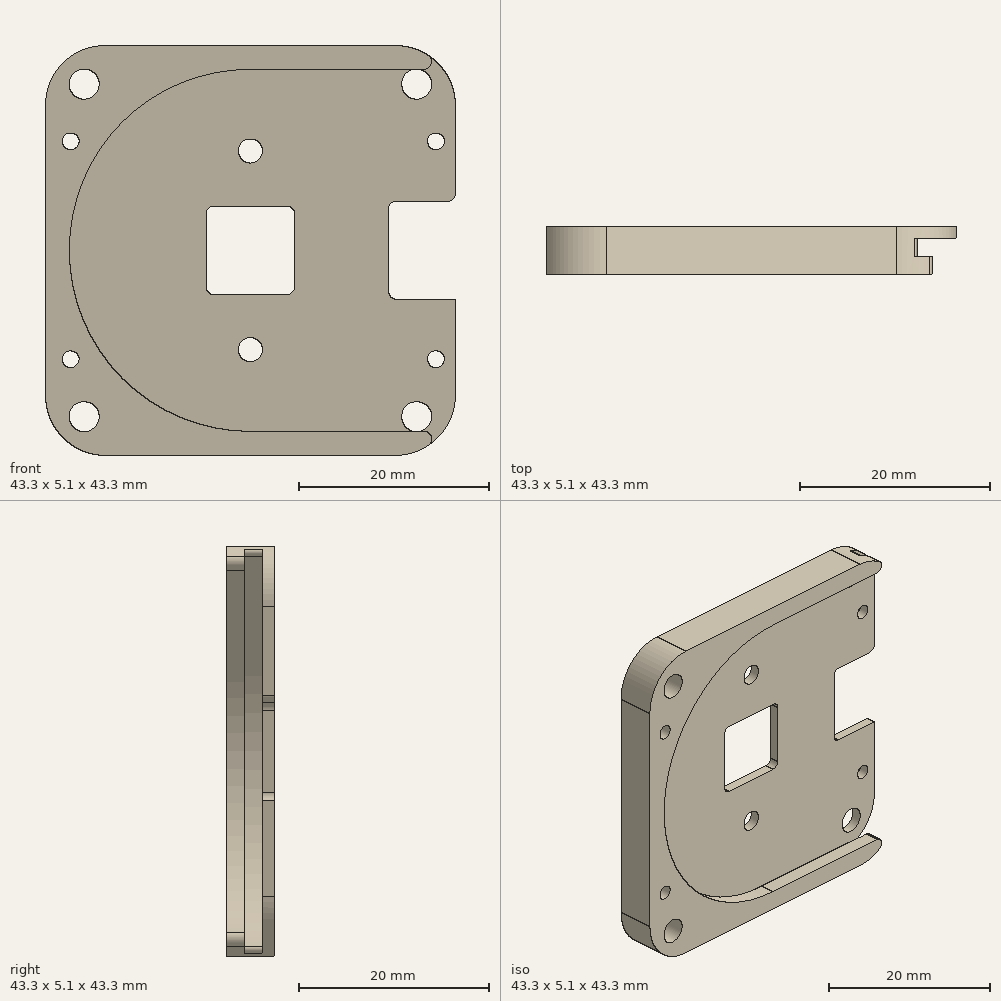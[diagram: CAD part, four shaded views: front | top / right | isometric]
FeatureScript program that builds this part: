
annotation { "Feature Type Name" : "Feature", "Feature Type Description" : "" }
export const myFeature = defineFeature(function(context is Context, id is Id, definition is map)
    precondition{}
    {
        {
            var Q0;
            Q0=qCreatedBy(makeId("Front.planeOp"),FACE);
            var sketch = newSketch(context, id + "F0", { "sketchPlane" : qUnion([Q0])});
            skLineSegment(sketch, "E0.bottom", {"start": v(0, 0) * mm, "end": v(43.3, 0) * mm});
            skLineSegment(sketch, "E0.top", {"start": v(0, 43.3) * mm, "end": v(43.3, 43.3) * mm});
            skLineSegment(sketch, "E0.left", {"start": v(0, 0) * mm, "end": v(0, 43.3) * mm});
            skLineSegment(sketch, "E0.right", {"start": v(43.3, 0) * mm, "end": v(43.3, 43.3) * mm});
            skSolve(sketch);
        }
        {
            var Q0;
            Q0=makeQuery(id+"F0.imprint","IMPRINT",FACE,{"disambiguationData":[TD([[makeQuery(id+"F0.imprint","IMPRINT",EDGE,{"derivedFrom":sQuery(id+"F0.wireOp",EDGE,"E0.bottom")}),1.0]])]});
            extrude(context, id + "F1", {"entities" : qUnion([Q0]), "depth" : 1.27 * mm});
        }
        {
            var Q0;
            Q0=qCreatedBy(makeId("Front.planeOp"),FACE);
            var sketch = newSketch(context, id + "F2", { "sketchPlane" : qUnion([Q0])});
            skLineSegment(sketch, "E1", {"start": v(0, 43.3) * mm, "end": v(43.3, 43.3) * mm});
            skLineSegment(sketch, "E2", {"start": v(43.3, 43.3) * mm, "end": v(43.3, 42.24) * mm});
            skLineSegment(sketch, "E3", {"start": v(43.3, 42.24) * mm, "end": v(21.64, 42.24) * mm});
            skLineSegment(sketch, "E4", {"start": v(0, 0) * mm, "end": v(43.3, 0) * mm});
            skLineSegment(sketch, "E5", {"start": v(43.3, 0) * mm, "end": v(43.3, 1.1) * mm});
            skLineSegment(sketch, "E6", {"start": v(43.3, 1.1) * mm, "end": v(21.64, 1.1) * mm});
            skArc(sketch, "E7", {"start": v(21.64, 42.24) * mm, "mid": v(1.07, 21.67) * mm, "end": v(21.64, 1.1) * mm});
            skLineSegment(sketch, "E8", {"start": v(0, 43.3) * mm, "end": v(0, 0) * mm});
            skSolve(sketch);
        }
        {
            var Q0;
            Q0=qSketchRegion(id+"F2",true);
            extrude(context, id + "F3", {"entities" : qUnion([Q0]), "operationType" : NewBodyOperationType.ADD, "depth" : 3.17 * mm});
        }
        {
            var Q0;
            Q0=makeQuery(id+"F3.opExtrude","CAP_FACE",FACE,{"disambiguationData":[OSD([sQuery(id+"F2.wireOp",EDGE,"E1"),sQuery(id+"F2.wireOp",EDGE,"E2"),sQuery(id+"F2.wireOp",EDGE,"E3"),sQuery(id+"F2.wireOp",EDGE,"E4"),sQuery(id+"F2.wireOp",EDGE,"E5"),sQuery(id+"F2.wireOp",EDGE,"E6"),sQuery(id+"F2.wireOp",EDGE,"E7"),sQuery(id+"F2.wireOp",EDGE,"E8")])],"isStart":false});
            var sketch = newSketch(context, id + "F4", { "sketchPlane" : qUnion([Q0])});
            skLineSegment(sketch, "E9", {"start": v(0, 43.3) * mm, "end": v(43.3, 43.3) * mm});
            skLineSegment(sketch, "E10", {"start": v(0, 43.3) * mm, "end": v(0, 0) * mm});
            skLineSegment(sketch, "E11", {"start": v(0, 0) * mm, "end": v(43.3, 0) * mm});
            skLineSegment(sketch, "E12", {"start": v(43.3, 0) * mm, "end": v(43.3, 2.54) * mm});
            skLineSegment(sketch, "E13", {"start": v(43.3, 2.54) * mm, "end": v(21.64, 2.54) * mm});
            skLineSegment(sketch, "E14", {"start": v(43.3, 43.3) * mm, "end": v(43.3, 40.8) * mm});
            skLineSegment(sketch, "E15", {"start": v(43.3, 40.8) * mm, "end": v(21.64, 40.8) * mm});
            skArc(sketch, "E16", {"start": v(21.64, 40.8) * mm, "mid": v(2.51, 21.67) * mm, "end": v(21.64, 2.54) * mm});
            skSolve(sketch);
        }
        {
            var Q0;
            Q0=qSketchRegion(id+"F4",true);
            extrude(context, id + "F5", {"entities" : qUnion([Q0]), "operationType" : NewBodyOperationType.ADD, "depth" : 1.9 * mm});
        }
        {
            var Q0;
            Q0=makeQuery(id+"F1.opExtrude","CAP_FACE",FACE,{"disambiguationData":[OSD([sQuery(id+"F0.wireOp",EDGE,"E0.bottom"),sQuery(id+"F0.wireOp",EDGE,"E0.top"),sQuery(id+"F0.wireOp",EDGE,"E0.left"),sQuery(id+"F0.wireOp",EDGE,"E0.right")])],"isStart":true});
            var sketch = newSketch(context, id + "F6", { "sketchPlane" : qUnion([Q0])});
            skCircle(sketch, "E17", {"center": v(-41.25, 33.17) * mm, "radius": 0.89 * mm});
            skCircle(sketch, "E18", {"center": v(-2.67, 33.17) * mm, "radius": 0.89 * mm});
            skCircle(sketch, "E19", {"center": v(-41.25, 10.16) * mm, "radius": 0.89 * mm});
            skCircle(sketch, "E20", {"center": v(-2.67, 10.16) * mm, "radius": 0.89 * mm});
            skSolve(sketch);
        }
        {
            var Q0;
            Q0=qSketchRegion(id+"F6",true);
            extrude(context, id + "F7", {"entities" : qUnion([Q0]), "operationType" : NewBodyOperationType.REMOVE, "endBound" : BoundingType.UP_TO_NEXT, "oppositeDirection" : true, "depth" : 25.4 * mm});
        }
        {
            var Q0;
            Q0=makeQuery(id+"F1.opExtrude","CAP_FACE",FACE,{"disambiguationData":[OSD([sQuery(id+"F0.wireOp",EDGE,"E0.bottom"),sQuery(id+"F0.wireOp",EDGE,"E0.top"),sQuery(id+"F0.wireOp",EDGE,"E0.left"),sQuery(id+"F0.wireOp",EDGE,"E0.right")])],"isStart":false});
            var sketch = newSketch(context, id + "F8", { "sketchPlane" : qUnion([Q0])});
            skLineSegment(sketch, "E21.bottom", {"start": v(17, 26.31) * mm, "end": v(26.31, 26.31) * mm});
            skLineSegment(sketch, "E21.top", {"start": v(17, 17) * mm, "end": v(26.31, 17) * mm});
            skLineSegment(sketch, "E21.left", {"start": v(17, 26.31) * mm, "end": v(17, 17) * mm});
            skLineSegment(sketch, "E21.right", {"start": v(26.31, 26.31) * mm, "end": v(26.31, 17) * mm});
            skLineSegment(sketch, "E22", {"start": v(43.3, 26.82) * mm, "end": v(36.25, 26.82) * mm});
            skLineSegment(sketch, "E23", {"start": v(36.25, 26.82) * mm, "end": v(36.25, 16.51) * mm});
            skLineSegment(sketch, "E24", {"start": v(36.25, 16.51) * mm, "end": v(43.3, 16.51) * mm});
            skLineSegment(sketch, "E25", {"start": v(43.3, 16.51) * mm, "end": v(43.3, 26.82) * mm});
            skSolve(sketch);
        }
        {
            var Q0;
            Q0=makeQuery(id+"F1.opExtrude","CAP_FACE",FACE,{"disambiguationData":[OSD([sQuery(id+"F0.wireOp",EDGE,"E0.bottom"),sQuery(id+"F0.wireOp",EDGE,"E0.top"),sQuery(id+"F0.wireOp",EDGE,"E0.left"),sQuery(id+"F0.wireOp",EDGE,"E0.right")])],"isStart":true});
            var sketch = newSketch(context, id + "F9", { "sketchPlane" : qUnion([Q0])});
            skPoint(sketch, "E26", {"position": v(-4.09, 39.22) * mm});
            skPoint(sketch, "E27", {"position": v(-39.22, 39.22) * mm});
            skPoint(sketch, "E28", {"position": v(-39.22, 4.09) * mm});
            skPoint(sketch, "E29", {"position": v(-4.09, 4.09) * mm});
            skSolve(sketch);
        }
        {
            var Q0;
            Q0=qSketchRegion(id+"F8",true);
            extrude(context, id + "F10", {"entities" : qUnion([Q0]), "operationType" : NewBodyOperationType.REMOVE, "endBound" : BoundingType.UP_TO_NEXT, "oppositeDirection" : true, "depth" : 25.4 * mm});
        }
        {
            var Q0;
            Q0=sQuery(id+"F9.wireOp",VERTEX,"E26");
            var Q1;
            Q1=sQuery(id+"F9.wireOp",VERTEX,"E29");
            var Q2;
            Q2=makeQuery(id+"F1.opExtrude","SWEPT_BODY",BODY,{"disambiguationData":[OSD([sQuery(id+"F0.wireOp",EDGE,"E0.bottom"),sQuery(id+"F0.wireOp",EDGE,"E0.top"),sQuery(id+"F0.wireOp",EDGE,"E0.left"),sQuery(id+"F0.wireOp",EDGE,"E0.right")])]});
            hole(context, id + "F11", {"style" : HoleStyle.SIMPLE, "endStyle" : HoleEndStyle.THROUGH, "holeDiameter" : 3.17 * mm, "isTappedThrough" : true, "tappedDepth" : 12.7 * mm, "tapClearance" : 3, "locations" : qUnion([Q0, Q1]), "scope" : qUnion([Q2])});
        }
        {
            var Q0;
            Q0=makeQuery(id+"F1.opExtrude","CAP_FACE",FACE,{"disambiguationData":[OSD([sQuery(id+"F0.wireOp",EDGE,"E0.bottom"),sQuery(id+"F0.wireOp",EDGE,"E0.top"),sQuery(id+"F0.wireOp",EDGE,"E0.left"),sQuery(id+"F0.wireOp",EDGE,"E0.right")])],"isStart":true});
            var sketch = newSketch(context, id + "F12", { "sketchPlane" : qUnion([Q0])});
            skLineSegment(sketch, "E30", {"start": v(-39.22, 39.22) * mm, "end": v(-4.09, 39.22) * mm, "construction": true});
            skLineSegment(sketch, "E31", {"start": v(-4.09, 39.22) * mm, "end": v(-4.09, 4.09) * mm, "construction": true});
            skLineSegment(sketch, "E32", {"start": v(-4.09, 4.09) * mm, "end": v(-39.22, 4.09) * mm, "construction": true});
            skLineSegment(sketch, "E33", {"start": v(-39.22, 4.09) * mm, "end": v(-39.22, 39.22) * mm, "construction": true});
            skSolve(sketch);
        }
        {
            var Q0;
            Q0=makeQuery(id+"F1.opExtrude","CAP_FACE",FACE,{"disambiguationData":[OSD([sQuery(id+"F0.wireOp",EDGE,"E0.bottom"),sQuery(id+"F0.wireOp",EDGE,"E0.top"),sQuery(id+"F0.wireOp",EDGE,"E0.left"),sQuery(id+"F0.wireOp",EDGE,"E0.right")])],"isStart":true});
            var sketch = newSketch(context, id + "F13", { "sketchPlane" : qUnion([Q0])});
            skLineSegment(sketch, "E34", {"start": v(-21.65, 32.16) * mm, "end": v(-21.65, 11.18) * mm});
            skPoint(sketch, "E34.startSnap0", {"position": v(-21.65, 26.31) * mm});
            skPoint(sketch, "E34.endSnap0", {"position": v(-21.65, 26.31) * mm});
            skSolve(sketch);
        }
        {
            var Q0;
            Q0=sQuery(id+"F13.wireOp",VERTEX,"E34.start");
            var Q1;
            Q1=sQuery(id+"F13.wireOp",VERTEX,"E34.end");
            var Q2;
            Q2=makeQuery(id+"F1.opExtrude","SWEPT_BODY",BODY,{"disambiguationData":[OSD([sQuery(id+"F0.wireOp",EDGE,"E0.bottom"),sQuery(id+"F0.wireOp",EDGE,"E0.top"),sQuery(id+"F0.wireOp",EDGE,"E0.left"),sQuery(id+"F0.wireOp",EDGE,"E0.right")])]});
            hole(context, id + "F14", {"style" : HoleStyle.SIMPLE, "endStyle" : HoleEndStyle.THROUGH, "holeDiameter" : 2.54 * mm, "isTappedThrough" : true, "tappedDepth" : 12.7 * mm, "tapClearance" : 3, "locations" : qUnion([Q0, Q1]), "scope" : qUnion([Q2])});
        }
        {
            var Q0;
            Q0=makeQuery(id+"F5.boolean.opBoolean","MERGE",EDGE,{"derivedFrom":[makeQuery(id+"F3.boolean.opBoolean","MERGE",EDGE,{"derivedFrom":[makeQuery(id+"F1.opExtrude","SWEPT_EDGE",EDGE,{"disambiguationData":[OSD([sQuery(id+"F0.wireOp",EDGE,"E0.top"),sQuery(id+"F0.wireOp",EDGE,"E0.left")])]}),makeQuery(id+"F3.opExtrude","SWEPT_EDGE",EDGE,{"disambiguationData":[OSD([sQuery(id+"F2.wireOp",EDGE,"E1"),sQuery(id+"F2.wireOp",EDGE,"E8")])]})]}),makeQuery(id+"F5.opExtrude","SWEPT_EDGE",EDGE,{"disambiguationData":[OSD([sQuery(id+"F4.wireOp",EDGE,"E9"),sQuery(id+"F4.wireOp",EDGE,"E10")])]})]});
            var Q1;
            Q1=makeQuery(id+"F5.boolean.opBoolean","MERGE",EDGE,{"derivedFrom":[makeQuery(id+"F3.boolean.opBoolean","MERGE",EDGE,{"derivedFrom":[makeQuery(id+"F1.opExtrude","SWEPT_EDGE",EDGE,{"disambiguationData":[OSD([sQuery(id+"F0.wireOp",EDGE,"E0.top"),sQuery(id+"F0.wireOp",EDGE,"E0.right")])]}),makeQuery(id+"F3.opExtrude","SWEPT_EDGE",EDGE,{"disambiguationData":[OSD([sQuery(id+"F2.wireOp",EDGE,"E1"),sQuery(id+"F2.wireOp",EDGE,"E2")])]})]}),makeQuery(id+"F5.opExtrude","SWEPT_EDGE",EDGE,{"disambiguationData":[OSD([sQuery(id+"F4.wireOp",EDGE,"E9"),sQuery(id+"F4.wireOp",EDGE,"E14")])]})]});
            var Q2;
            Q2=makeQuery(id+"F5.boolean.opBoolean","MERGE",EDGE,{"derivedFrom":[makeQuery(id+"F3.boolean.opBoolean","MERGE",EDGE,{"derivedFrom":[makeQuery(id+"F1.opExtrude","SWEPT_EDGE",EDGE,{"disambiguationData":[OSD([sQuery(id+"F0.wireOp",EDGE,"E0.bottom"),sQuery(id+"F0.wireOp",EDGE,"E0.right")])]}),makeQuery(id+"F3.opExtrude","SWEPT_EDGE",EDGE,{"disambiguationData":[OSD([sQuery(id+"F2.wireOp",EDGE,"E4"),sQuery(id+"F2.wireOp",EDGE,"E5")])]})]}),makeQuery(id+"F5.opExtrude","SWEPT_EDGE",EDGE,{"disambiguationData":[OSD([sQuery(id+"F4.wireOp",EDGE,"E11"),sQuery(id+"F4.wireOp",EDGE,"E12")])]})]});
            var Q3;
            Q3=makeQuery(id+"F5.boolean.opBoolean","MERGE",EDGE,{"derivedFrom":[makeQuery(id+"F3.boolean.opBoolean","MERGE",EDGE,{"derivedFrom":[makeQuery(id+"F1.opExtrude","SWEPT_EDGE",EDGE,{"disambiguationData":[OSD([sQuery(id+"F0.wireOp",EDGE,"E0.bottom"),sQuery(id+"F0.wireOp",EDGE,"E0.left")])]}),makeQuery(id+"F3.opExtrude","SWEPT_EDGE",EDGE,{"disambiguationData":[OSD([sQuery(id+"F2.wireOp",EDGE,"E4"),sQuery(id+"F2.wireOp",EDGE,"E8")])]})]}),makeQuery(id+"F5.opExtrude","SWEPT_EDGE",EDGE,{"disambiguationData":[OSD([sQuery(id+"F4.wireOp",EDGE,"E10"),sQuery(id+"F4.wireOp",EDGE,"E11")])]})]});
            fillet(context, id + "F15", {"entities" : qUnion([Q0, Q1, Q2, Q3]), "radius" : 6.35 * mm, "tangentPropagation" : true, "allowEdgeOverflow" : false});
        }
        {
            var Q0;
            {var subQ1=sQuery(id+"F4.wireOp",EDGE,"E15");var subQ2=sQuery(id+"F4.wireOp",EDGE,"E14");var subQ7=sQuery(id+"F4.wireOp",EDGE,"E9");var subQ8=sQuery(id+"F2.wireOp",EDGE,"E2");var subQ9=sQuery(id+"F0.wireOp",EDGE,"E0.right");Q0=makeQuery(id+"F15.opFillet","BLEND_EDGE",EDGE,{"blendedFrom":[makeQuery(id+"F5.boolean.opBoolean","MERGE",EDGE,{"derivedFrom":[makeQuery(id+"F3.boolean.opBoolean","MERGE",EDGE,{"derivedFrom":[makeQuery(id+"F1.opExtrude","SWEPT_EDGE",EDGE,{"disambiguationData":[OSD([sQuery(id+"F0.wireOp",EDGE,"E0.top"),subQ9])]}),makeQuery(id+"F3.opExtrude","SWEPT_EDGE",EDGE,{"disambiguationData":[OSD([sQuery(id+"F2.wireOp",EDGE,"E1"),subQ8])]})]}),makeQuery(id+"F5.opExtrude","SWEPT_EDGE",EDGE,{"disambiguationData":[OSD([subQ7,subQ2])]})]}),makeQuery(id+"FAVqUnOOAbN4NIG_1.hole-0.boolean.opBoolean","SPLIT",FACE,{"disambiguationData":[TD([makeQuery(id+"F1.opExtrude","SWEPT_FACE",FACE,{"disambiguationData":[OSD([subQ9])]})])],"derivedFrom":makeQuery(id+"F5.opExtrude","SWEPT_FACE",FACE,{"disambiguationData":[OSD([subQ1])]})})],"blendedInto":[makeQuery(id+"FAVqUnOOAbN4NIG_1.hole-0.boolean.opBoolean","SPLIT",FACE,{"disambiguationData":[TD([makeQuery(id+"F1.opExtrude","SWEPT_FACE",FACE,{"disambiguationData":[OSD([subQ9])]})])],"derivedFrom":makeQuery(id+"F5.opExtrude","SWEPT_FACE",FACE,{"disambiguationData":[OSD([subQ1])]})})]});}
            var Q1;
            {var subQ3=sQuery(id+"F4.wireOp",EDGE,"E13");var subQ4=sQuery(id+"F4.wireOp",EDGE,"E12");var subQ5=sQuery(id+"F4.wireOp",EDGE,"E11");var subQ8=sQuery(id+"F2.wireOp",EDGE,"E5");var subQ9=sQuery(id+"F0.wireOp",EDGE,"E0.right");Q1=makeQuery(id+"F15.opFillet","BLEND_EDGE",EDGE,{"blendedFrom":[makeQuery(id+"F5.boolean.opBoolean","MERGE",EDGE,{"derivedFrom":[makeQuery(id+"F3.boolean.opBoolean","MERGE",EDGE,{"derivedFrom":[makeQuery(id+"F1.opExtrude","SWEPT_EDGE",EDGE,{"disambiguationData":[OSD([sQuery(id+"F0.wireOp",EDGE,"E0.bottom"),subQ9])]}),makeQuery(id+"F3.opExtrude","SWEPT_EDGE",EDGE,{"disambiguationData":[OSD([sQuery(id+"F2.wireOp",EDGE,"E4"),subQ8])]})]}),makeQuery(id+"F5.opExtrude","SWEPT_EDGE",EDGE,{"disambiguationData":[OSD([subQ5,subQ4])]})]}),makeQuery(id+"FAVqUnOOAbN4NIG_1.hole-3.boolean.opBoolean","SPLIT",FACE,{"disambiguationData":[TD([makeQuery(id+"F1.opExtrude","SWEPT_FACE",FACE,{"disambiguationData":[OSD([subQ9])]})])],"derivedFrom":makeQuery(id+"F5.opExtrude","SWEPT_FACE",FACE,{"disambiguationData":[OSD([subQ3])]})})],"blendedInto":[makeQuery(id+"FAVqUnOOAbN4NIG_1.hole-3.boolean.opBoolean","SPLIT",FACE,{"disambiguationData":[TD([makeQuery(id+"F1.opExtrude","SWEPT_FACE",FACE,{"disambiguationData":[OSD([subQ9])]})])],"derivedFrom":makeQuery(id+"F5.opExtrude","SWEPT_FACE",FACE,{"disambiguationData":[OSD([subQ3])]})})]});}
            fillet(context, id + "F16", {"entities" : qUnion([Q0, Q1]), "radius" : 0.81 * mm, "tangentPropagation" : true, "allowEdgeOverflow" : false});
        }
        {
            var Q0;
            Q0=makeQuery(id+"F10.boolean.opBoolean","COPY",EDGE,{"derivedFrom":makeQuery(id+"F10.opExtrude","SWEPT_EDGE",EDGE,{"disambiguationData":[OSD([sQuery(id+"F0.wireOp",EDGE,"E0.right"),sQuery(id+"F8.wireOp",EDGE,"E22"),sQuery(id+"F8.wireOp",EDGE,"E25")])]})});
            var Q1;
            Q1=makeQuery(id+"F10.boolean.opBoolean","COPY",EDGE,{"derivedFrom":makeQuery(id+"F10.opExtrude","SWEPT_EDGE",EDGE,{"disambiguationData":[OSD([sQuery(id+"F8.wireOp",EDGE,"E22"),sQuery(id+"F8.wireOp",EDGE,"E23")])]})});
            var Q2;
            Q2=makeQuery(id+"F10.boolean.opBoolean","COPY",EDGE,{"derivedFrom":makeQuery(id+"F10.opExtrude","SWEPT_EDGE",EDGE,{"disambiguationData":[OSD([sQuery(id+"F8.wireOp",EDGE,"E21.bottom"),sQuery(id+"F8.wireOp",EDGE,"E21.left")])]})});
            var Q3;
            Q3=makeQuery(id+"F10.boolean.opBoolean","COPY",EDGE,{"derivedFrom":makeQuery(id+"F10.opExtrude","SWEPT_EDGE",EDGE,{"disambiguationData":[OSD([sQuery(id+"F8.wireOp",EDGE,"E21.top"),sQuery(id+"F8.wireOp",EDGE,"E21.left")])]})});
            var Q4;
            Q4=makeQuery(id+"F10.boolean.opBoolean","COPY",EDGE,{"derivedFrom":makeQuery(id+"F10.opExtrude","SWEPT_EDGE",EDGE,{"disambiguationData":[OSD([sQuery(id+"F8.wireOp",EDGE,"E21.top"),sQuery(id+"F8.wireOp",EDGE,"E21.right")])]})});
            var Q5;
            Q5=makeQuery(id+"F10.boolean.opBoolean","COPY",EDGE,{"derivedFrom":makeQuery(id+"F10.opExtrude","SWEPT_EDGE",EDGE,{"disambiguationData":[OSD([sQuery(id+"F0.wireOp",EDGE,"E0.right"),sQuery(id+"F8.wireOp",EDGE,"E24"),sQuery(id+"F8.wireOp",EDGE,"E25")])]})});
            var Q6;
            Q6=makeQuery(id+"F10.boolean.opBoolean","COPY",EDGE,{"derivedFrom":makeQuery(id+"F10.opExtrude","SWEPT_EDGE",EDGE,{"disambiguationData":[OSD([sQuery(id+"F8.wireOp",EDGE,"E23"),sQuery(id+"F8.wireOp",EDGE,"E24")])]})});
            var Q7;
            Q7=makeQuery(id+"F10.boolean.opBoolean","COPY",EDGE,{"derivedFrom":makeQuery(id+"F10.opExtrude","SWEPT_EDGE",EDGE,{"disambiguationData":[OSD([sQuery(id+"F8.wireOp",EDGE,"E21.bottom"),sQuery(id+"F8.wireOp",EDGE,"E21.right")])]})});
            fillet(context, id + "F17", {"entities" : qUnion([Q0, Q1, Q2, Q3, Q4, Q5, Q6, Q7]), "radius" : 0.79 * mm, "tangentPropagation" : true, "allowEdgeOverflow" : false});
        }
        {
            var Q0;
            Q0=sQuery(id+"F12.wireOp",VERTEX,"E33.start");
            var Q1;
            Q1=sQuery(id+"F12.wireOp",VERTEX,"E33.end");
            var Q2;
            Q2=makeQuery(id+"F1.opExtrude","SWEPT_BODY",BODY,{"disambiguationData":[OSD([sQuery(id+"F0.wireOp",EDGE,"E0.bottom"),sQuery(id+"F0.wireOp",EDGE,"E0.top"),sQuery(id+"F0.wireOp",EDGE,"E0.left"),sQuery(id+"F0.wireOp",EDGE,"E0.right")])]});
            hole(context, id + "F18", {"style" : HoleStyle.SIMPLE, "endStyle" : HoleEndStyle.BLIND, "holeDiameter" : 3.17 * mm, "holeDepth" : 3.17 * mm, "isTappedThrough" : true, "tappedDepth" : 12.7 * mm, "tapClearance" : 3, "locations" : qUnion([Q0, Q1]), "scope" : qUnion([Q2])});
        }
        {
            var Q0;
            Q0=makeQuery(id+"F16.opFillet","BLEND_EDGE",EDGE,{"blendedFrom":[makeQuery(id+"F15.opFillet","BLEND_EDGE",EDGE,{"blendedFrom":[makeQuery(id+"F5.boolean.opBoolean","MERGE",EDGE,{"derivedFrom":[makeQuery(id+"F3.boolean.opBoolean","MERGE",EDGE,{"derivedFrom":[makeQuery(id+"F1.opExtrude","SWEPT_EDGE",EDGE,{"disambiguationData":[OSD([sQuery(id+"F0.wireOp",EDGE,"E0.top"),sQuery(id+"F0.wireOp",EDGE,"E0.right")])]}),makeQuery(id+"F3.opExtrude","SWEPT_EDGE",EDGE,{"disambiguationData":[OSD([sQuery(id+"F2.wireOp",EDGE,"E1"),sQuery(id+"F2.wireOp",EDGE,"E2")])]})]}),makeQuery(id+"F5.opExtrude","SWEPT_EDGE",EDGE,{"disambiguationData":[OSD([sQuery(id+"F4.wireOp",EDGE,"E9"),sQuery(id+"F4.wireOp",EDGE,"E14")])]})]}),makeQuery(id+"F5.opExtrude","SWEPT_FACE",FACE,{"disambiguationData":[OSD([sQuery(id+"F4.wireOp",EDGE,"E15")])]})],"blendedInto":[makeQuery(id+"F5.opExtrude","SWEPT_FACE",FACE,{"disambiguationData":[OSD([sQuery(id+"F4.wireOp",EDGE,"E15")])]})]}),makeQuery(id+"F3.opExtrude","SWEPT_FACE",FACE,{"disambiguationData":[OSD([sQuery(id+"F2.wireOp",EDGE,"E3")])]})],"blendedInto":[makeQuery(id+"F3.opExtrude","SWEPT_FACE",FACE,{"disambiguationData":[OSD([sQuery(id+"F2.wireOp",EDGE,"E3")])]})]});
            var Q1;
            Q1=makeQuery(id+"F16.opFillet","BLEND_EDGE",EDGE,{"blendedFrom":[makeQuery(id+"F15.opFillet","BLEND_EDGE",EDGE,{"blendedFrom":[makeQuery(id+"F5.boolean.opBoolean","MERGE",EDGE,{"derivedFrom":[makeQuery(id+"F3.boolean.opBoolean","MERGE",EDGE,{"derivedFrom":[makeQuery(id+"F1.opExtrude","SWEPT_EDGE",EDGE,{"disambiguationData":[OSD([sQuery(id+"F0.wireOp",EDGE,"E0.bottom"),sQuery(id+"F0.wireOp",EDGE,"E0.right")])]}),makeQuery(id+"F3.opExtrude","SWEPT_EDGE",EDGE,{"disambiguationData":[OSD([sQuery(id+"F2.wireOp",EDGE,"E4"),sQuery(id+"F2.wireOp",EDGE,"E5")])]})]}),makeQuery(id+"F5.opExtrude","SWEPT_EDGE",EDGE,{"disambiguationData":[OSD([sQuery(id+"F4.wireOp",EDGE,"E11"),sQuery(id+"F4.wireOp",EDGE,"E12")])]})]}),makeQuery(id+"F5.opExtrude","SWEPT_FACE",FACE,{"disambiguationData":[OSD([sQuery(id+"F4.wireOp",EDGE,"E13")])]})],"blendedInto":[makeQuery(id+"F5.opExtrude","SWEPT_FACE",FACE,{"disambiguationData":[OSD([sQuery(id+"F4.wireOp",EDGE,"E13")])]})]}),makeQuery(id+"F3.opExtrude","SWEPT_FACE",FACE,{"disambiguationData":[OSD([sQuery(id+"F2.wireOp",EDGE,"E6")])]})],"blendedInto":[makeQuery(id+"F3.opExtrude","SWEPT_FACE",FACE,{"disambiguationData":[OSD([sQuery(id+"F2.wireOp",EDGE,"E6")])]})]});
            fillet(context, id + "F19", {"entities" : qUnion([Q0, Q1]), "radius" : 0.4 * mm, "tangentPropagation" : true, "allowEdgeOverflow" : false});
        }
    });
